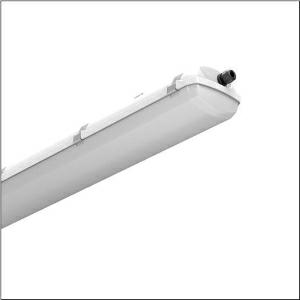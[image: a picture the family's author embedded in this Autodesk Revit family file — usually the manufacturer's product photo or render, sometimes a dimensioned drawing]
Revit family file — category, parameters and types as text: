
# Revit family: monsun_r__ex_51fxa27l860a_0ded
name_source: partatom
category: Lighting Fixtures
units: mm (PartAtom-declared; Revit-internal decimal feet)

## family parameters
Cut with Voids When Loaded = No
Host = Face
Light Source = No
Part Type = Normal
Room Calculation Point = No
Round Connector Dimension = Use Diameter
Shared = No

## types (1)
- Monsun® Ex (1 x LED, 6560 lm, 53 W, 6500K)
    Apparent Load = 53 VA
    CIE Flux Codes = 46 76 94 98 100
    Color Rendering = 80
    Color Temperature = 6500K
    Default Elevation = 1800 mm
    Description = Monsun® Ex, damp-proof luminaire, primary optical cover: cover, of PC, UV-stabilised, opal, light emission: direct distribution, primary light characteristic: symmetric, installation type: surface-mounted, LED, rated luminous flux: 6.560lm, luminous efficacy: 124lm/W, light colour: 860, colour temperature: 6000K, control gear: ON/OFF, with terminal, 3-pole, max. 2.5mm², through-wiring: 5x 2.5mm², mains connection: 220..250V, AC, 50/60Hz, rated input power: 53W, housing, of PC, light grey (RAL 7035), incl. 1x Ex cable gland M20 for cable diameter 7..12mm with sealing, incl. 1x Ex locking screw M20 with sealing, length: 1.280mm, width: 155mm, height: 105mm, clip for enclosure, of stainless steel, protection rating (complete): IP66, insulation class (complete): insulation class I (protective earthing), certification: CE, explosion class: zone 1,21 II 2G Ex eb mb op is IIC T4 Gb, II 2D Ex tb op is IIIC T67°C Db, impact resistance: IK10, permissible operating ambient temperature: -20..+40°C, contact your sales advisor before using the luminaires in applications with unclear chemical exposure, large temperature fluctuations or condensation-forming humidity, packaging unit: 1 piece
    Height = 105 mm
    Lamp = 1 x LED
    Lamp Light Flux = 6560 lm
    Lamp Power = 53 W
    Lamp count = 1
    Length = 1280 mm
    Luminous efficacy = 124 lm/W
    Manufacturer = Siteco
    ModVariant = No
    Model = 51FXA27L860A
    Mounting Place = Ceiling
    Mounting Type = Surface mounted
    Number of Poles = 1
    OnlyDefault = Yes
    Power Factor = 1
    Product Name = Monsun® Ex
    Product group = damp-proof luminaire
    ProductGroupID = 300
    Protection Class = Protection class I
    Protection Degree = IP 66
    RLX_Detail_Level = 1
    RLX_Emergency_Light_Flux = 0 lm
    RLX_Emergency_Type = 0
    RLX_Emergency_Type_DB = No
    RlxData = <blob elided: 41697 chars, md5=5f0ae7f8>
    Socket = socket
    Standby Power = 0 W
    System Light Flux = 6560 lm
    System Power = 53 W
    Type Comments = Product without accessories
    Type Image = l_1258882.jpg
    URL = http://relux.com
    VarID = ---
    Voltage = 0 V
    Weight = 0.00 kg
    Width = 155 mm

## geometry (parser evidence)
native form markers: Blend x4, Sweep x10
no freeform markers — native parametric forms only
